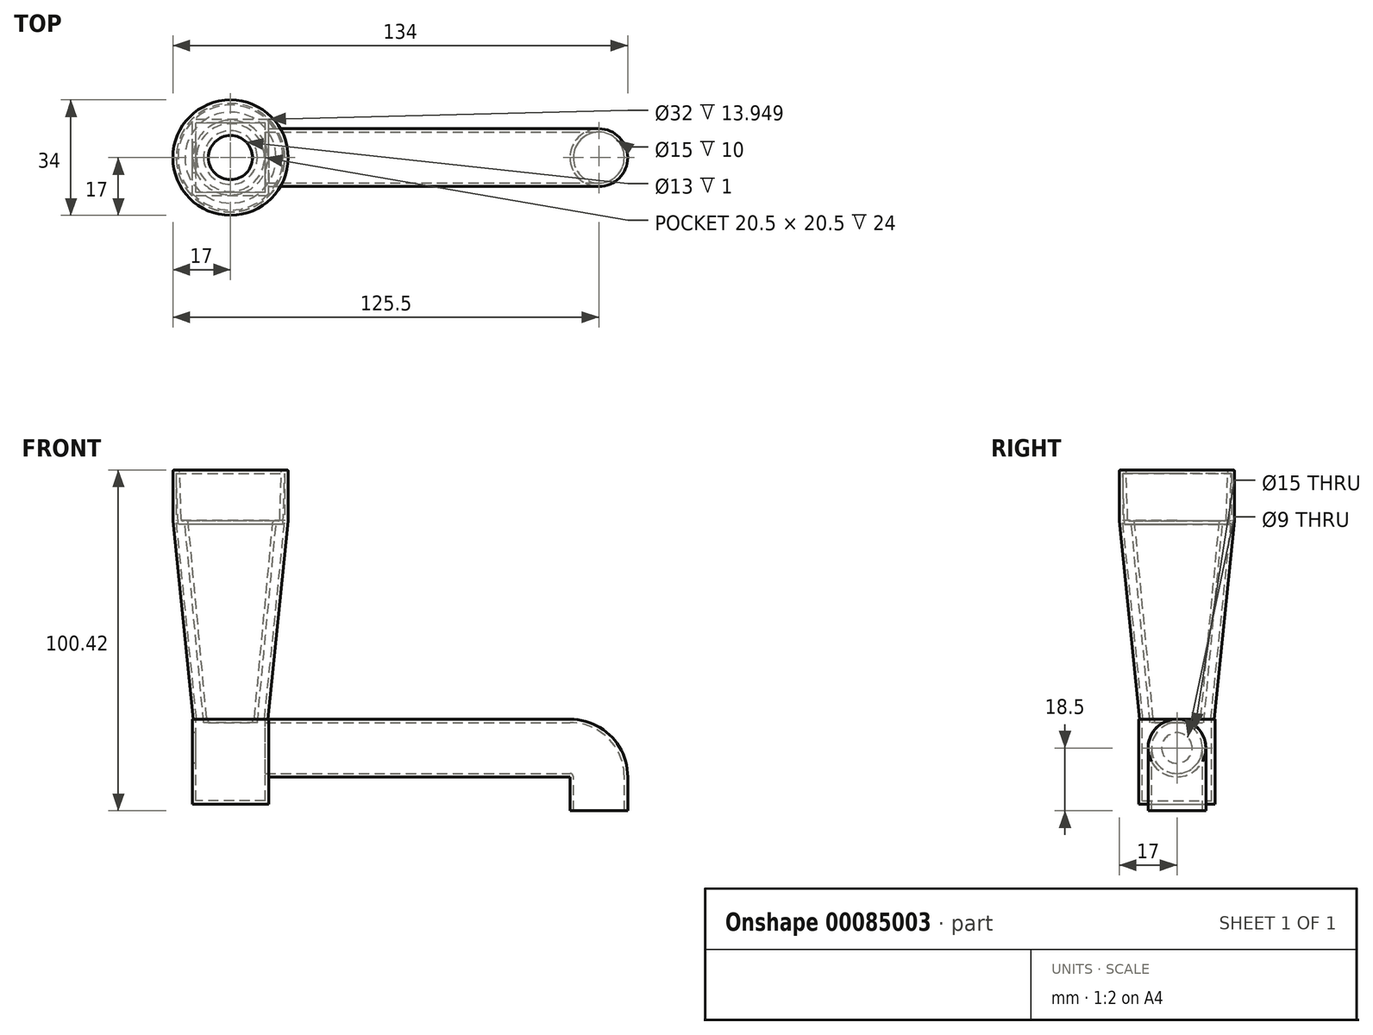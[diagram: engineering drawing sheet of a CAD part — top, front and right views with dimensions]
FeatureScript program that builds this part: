
annotation { "Feature Type Name" : "Feature", "Feature Type Description" : "" }
export const myFeature = defineFeature(function(context is Context, id is Id, definition is map)
    precondition{}
    {
        {
            var Q0;
            Q0=qCreatedBy(makeId("Front.planeOp"),FACE);
            var sketch = newSketch(context, id + "F0", { "sketchPlane" : qUnion([Q0])});
            skLineSegment(sketch, "E0", {"start": v(0, 0) * mm, "end": v(0, 73.42) * mm, "construction": true});
            skLineSegment(sketch, "E1", {"start": v(0, 73.42) * mm, "end": v(15, 73.42) * mm, "construction": true});
            skLineSegment(sketch, "E2", {"start": v(15, 73.42) * mm, "end": v(17, 73.42) * mm});
            skLineSegment(sketch, "E3", {"start": v(17, 73.42) * mm, "end": v(17, 58.42) * mm});
            skLineSegment(sketch, "E4", {"start": v(0, 58.42) * mm, "end": v(14.5, 58.42) * mm, "construction": true});
            skLineSegment(sketch, "E5", {"start": v(15, 73.42) * mm, "end": v(14.5, 58.42) * mm});
            skLineSegment(sketch, "E6", {"start": v(14.5, 58.42) * mm, "end": v(12.5, 58.42) * mm});
            skLineSegment(sketch, "E7", {"start": v(0, 0) * mm, "end": v(7, 0) * mm, "construction": true});
            skLineSegment(sketch, "E8", {"start": v(12.5, 58.42) * mm, "end": v(7, 0) * mm});
            skLineSegment(sketch, "E9", {"start": v(17, 58.42) * mm, "end": v(11, 0) * mm});
            skLineSegment(sketch, "E10", {"start": v(11, 0) * mm, "end": v(7, 0) * mm});
            skSolve(sketch);
        }
        {
            var Q0;
            Q0 = qSketchRegion(id + "F0", true);
            var Q1;
            Q1=sQuery(id+"F0.wireOp",EDGE,"E0");
            revolve(context, id + "F1", {"entities" : qUnion([Q0]), "axis" : qUnion([Q1]), "revolveType" : RevolveType.FULL});
        }
        {
            var Q0;
            Q0=qCreatedBy(makeId("Right.planeOp"),FACE);
            cPlane(context, id + "F2", {"entities" : qUnion([Q0]), "cplaneType" : CPlaneType.OFFSET, "offset" : 100 * mm, "width" : 150 * mm, "height" : 150 * mm});
        }
        {
            var Q0;
            Q0=makeQuery(id+"F1.opRevolve","SWEPT_FACE",FACE,{"disambiguationData":[OSD([sQuery(id+"F0.wireOp",EDGE,"E10")])]});
            var sketch = newSketch(context, id + "F3", { "sketchPlane" : qUnion([Q0])});
            skLineSegment(sketch, "E11.bottom", {"start": v(11.25, 11.25) * mm, "end": v(-11.25, 11.25) * mm});
            skLineSegment(sketch, "E11.top", {"start": v(11.25, -11.25) * mm, "end": v(-11.25, -11.25) * mm});
            skLineSegment(sketch, "E11.left", {"start": v(11.25, 11.25) * mm, "end": v(11.25, -11.25) * mm});
            skLineSegment(sketch, "E11.right", {"start": v(-11.25, 11.25) * mm, "end": v(-11.25, -11.25) * mm});
            skPoint(sketch, "E11.middle", {"position": v(0, 0) * mm});
            skSolve(sketch);
        }
        {
            var Q0;
            Q0 = qSketchRegion(id + "F3", true);
            extrude(context, id + "F4", {"entities" : qUnion([Q0]), "operationType" : NewBodyOperationType.ADD, "depth" : 25 * mm});
        }
        {
            var Q0;
            {var subQ0=sQuery(id+"F3.wireOp",EDGE,"E11.left");var subQ1=sQuery(id+"F3.wireOp",EDGE,"E11.top");var subQ2=sQuery(id+"F3.wireOp",EDGE,"E11.bottom");var subQ3=sQuery(id+"F3.wireOp",EDGE,"E11.right");Q0=makeQuery(id+"F4.boolean.opBoolean","SPLIT",FACE,{"disambiguationData":[TD([makeQuery(id+"F1.opRevolve","SWEPT_FACE",FACE,{"disambiguationData":[OSD([sQuery(id+"F0.wireOp",EDGE,"E9")])]})])],"derivedFrom":makeQuery(id+"F4.opExtrude","CAP_FACE",FACE,{"disambiguationData":[OSD([subQ2,subQ1,subQ0,subQ3])],"isStart":true})});}
            shell(context, id + "F5", {"entities" : qUnion([Q0]), "thickness" : 1 * mm});
        }
        {
            var Q0;
            Q0=qCreatedBy(id+"F2.planeOp",FACE);
            var sketch = newSketch(context, id + "F6", { "sketchPlane" : qUnion([Q0])});
            skCircle(sketch, "E12", {"center": v(0, -8.5) * mm, "radius": 8.5 * mm});
            skCircle(sketch, "E13", {"center": v(0, -8.5) * mm, "radius": 7.5 * mm});
            skSolve(sketch);
        }
        {
            var Q0;
            Q0 = qSketchRegion(id + "F6", true);
            extrude(context, id + "F7", {"entities" : qUnion([Q0]), "operationType" : NewBodyOperationType.ADD, "endBound" : BoundingType.UP_TO_NEXT, "oppositeDirection" : true, "depth" : 100 * mm});
        }
        {
            var Q0;
            Q0=makeQuery(id+"F1.opRevolve","SWEPT_EDGE",EDGE,{"disambiguationData":[OSD([sQuery(id+"F0.wireOp",EDGE,"E2"),sQuery(id+"F0.wireOp",EDGE,"E5")])]});
            var Q1;
            Q1=makeQuery(id+"F1.opRevolve","SWEPT_EDGE",EDGE,{"disambiguationData":[OSD([sQuery(id+"F0.wireOp",EDGE,"E2"),sQuery(id+"F0.wireOp",EDGE,"E3")])]});
            var Q2;
            Q2=makeQuery(id+"F1.opRevolve","SWEPT_EDGE",EDGE,{"disambiguationData":[OSD([sQuery(id+"F0.wireOp",EDGE,"E6"),sQuery(id+"F0.wireOp",EDGE,"E8")])]});
            var Q3;
            Q3=makeQuery(id+"F1.opRevolve","SWEPT_EDGE",EDGE,{"disambiguationData":[OSD([sQuery(id+"F0.wireOp",EDGE,"E5"),sQuery(id+"F0.wireOp",EDGE,"E6")])]});
            var Q4;
            Q4=makeQuery(id+"F1.opRevolve","SWEPT_EDGE",EDGE,{"disambiguationData":[OSD([sQuery(id+"F0.wireOp",EDGE,"E3"),sQuery(id+"F0.wireOp",EDGE,"E9")])]});
            var Q5;
            Q5=makeQuery(id+"F1.opRevolve","SWEPT_EDGE",EDGE,{"disambiguationData":[OSD([sQuery(id+"F0.wireOp",EDGE,"E9"),sQuery(id+"F0.wireOp",EDGE,"HRKtv9Oi-gNw8-WM0d-tN7Y-wkfImeTK1ehS")])]});
            var Q6;
            Q6=makeQuery(id+"F7.opExtrude","TWEAK_EDGE",EDGE,{"derivedFrom":[makeQuery(id+"F1.opRevolve","SWEPT_FACE",FACE,{"disambiguationData":[OSD([sQuery(id+"F0.wireOp",EDGE,"E9")])]}),makeQuery(id+"F6.imprint","IMPRINT",EDGE,{"derivedFrom":sQuery(id+"F6.wireOp",EDGE,"6v9iyHCW-eKOX-CDvE-R3rD-riR51iMcDnOg")})]});
            var Q7;
            Q7=makeQuery(id+"F7.opExtrude","SWEPT_FACE",FACE,{"disambiguationData":[OSD([sQuery(id+"F6.wireOp",EDGE,"6v9iyHCW-eKOX-CDvE-R3rD-riR51iMcDnOg")])]});
            fillet(context, id + "F8", {"entities" : qUnion([Q0, Q1, Q2, Q3, Q4, Q5, Q6, Q7]), "radius" : 0.5 * mm, "tangentPropagation" : true, "allowEdgeOverflow" : false});
        }
        {
            var Q0;
            Q0=makeQuery(id+"F1.opRevolve","SWEPT_EDGE",EDGE,{"disambiguationData":[OSD([sQuery(id+"F0.wireOp",EDGE,"HRKtv9Oi-gNw8-WM0d-tN7Y-wkfImeTK1ehS"),sQuery(id+"F0.wireOp",EDGE,"E10")])]});
            fillet(context, id + "F9", {"entities" : qUnion([Q0]), "radius" : 0.5 * mm, "tangentPropagation" : true, "allowEdgeOverflow" : false});
        }
        {
            var Q0;
            Q0=makeQuery(id+"F6.imprint","IMPRINT",FACE,{"disambiguationData":[TD([[makeQuery(id+"F6.imprint","IMPRINT",EDGE,{"derivedFrom":sQuery(id+"F6.wireOp",EDGE,"E12")}),1.0]])]});
            var sketch = newSketch(context, id + "F10", { "sketchPlane" : qUnion([Q0])});
            skCircle(sketch, "E14", {"center": v(0, -8.5) * mm, "radius": 7.5 * mm});
            skSolve(sketch);
        }
        {
            var Q0;
            Q0 = qSketchRegion(id + "F10", true);
            extrude(context, id + "F11", {"entities" : qUnion([Q0]), "operationType" : NewBodyOperationType.REMOVE, "oppositeDirection" : true, "depth" : 96.68 * mm});
        }
        {
            var Q0;
            Q0=qCreatedBy(makeId("Right.planeOp"),FACE);
            cPlane(context, id + "F12", {"entities" : qUnion([Q0]), "cplaneType" : CPlaneType.OFFSET, "offset" : 50 * mm, "oppositeDirection" : true, "width" : 150 * mm, "height" : 150 * mm});
        }
        {
            var Q0;
            Q0=qCreatedBy(id+"F12.planeOp",FACE);
            var sketch = newSketch(context, id + "F13", { "sketchPlane" : qUnion([Q0])});
            skCircle(sketch, "E15", {"center": v(0, -8.5) * mm, "radius": 4.5 * mm});
            skSolve(sketch);
        }
        {
            var Q0;
            Q0 = qSketchRegion(id + "F13", true);
            extrude(context, id + "F14", {"entities" : qUnion([Q0]), "operationType" : NewBodyOperationType.REMOVE, "depth" : 45.83 * mm});
        }
        {
            var Q0;
            Q0=qCreatedBy(id+"F2.planeOp",FACE);
            var sketch = newSketch(context, id + "F15", { "sketchPlane" : qUnion([Q0])});
            skLineSegment(sketch, "E16", {"start": v(-11.2, -17) * mm, "end": v(11.3, -17) * mm, "construction": true});
            skCircle(sketch, "E17", {"center": v(0, -8.5) * mm, "radius": 8.5 * mm});
            skCircle(sketch, "E18", {"center": v(0, -8.5) * mm, "radius": 7.5 * mm});
            skSolve(sketch);
        }
        {
            var Q0;
            Q0 = qSketchRegion(id + "F15", true);
            var Q1;
            Q1=sQuery(id+"F15.wireOp",EDGE,"E16");
            revolve(context, id + "F16", {"operationType" : NewBodyOperationType.ADD, "entities" : qUnion([Q0]), "axis" : qUnion([Q1]), "revolveType" : RevolveType.ONE_DIRECTION, "angle" : 90 * degree});
        }
        {
            var Q0;
            Q0=makeQuery(id+"F16.opRevolve","CAP_FACE",FACE,{"disambiguationData":[OSD([sQuery(id+"F15.wireOp",EDGE,"E17"),sQuery(id+"F15.wireOp",EDGE,"E18")])],"isStart":false});
            var sketch = newSketch(context, id + "F17", { "sketchPlane" : qUnion([Q0])});
            skCircle(sketch, "E19", {"center": v(108.5, 0) * mm, "radius": 8.5 * mm});
            skCircle(sketch, "E20", {"center": v(108.5, 0) * mm, "radius": 7.5 * mm});
            skSolve(sketch);
        }
        {
            var Q0;
            Q0 = qSketchRegion(id + "F17", true);
            extrude(context, id + "F18", {"entities" : qUnion([Q0]), "operationType" : NewBodyOperationType.ADD, "depth" : 10 * mm});
        }
        {
            var Q0;
            Q0=qCreatedBy(makeId("Top.planeOp"),FACE);
            cPlane(context, id + "F19", {"entities" : qUnion([Q0]), "cplaneType" : CPlaneType.OFFSET, "offset" : 150 * mm, "width" : 150 * mm, "height" : 150 * mm});
        }
        {
            var Q0;
            Q0=qCreatedBy(id+"F19.planeOp",FACE);
            var sketch = newSketch(context, id + "F20", { "sketchPlane" : qUnion([Q0])});
            skCircle(sketch, "E21", {"center": v(0, 0) * mm, "radius": 6.5 * mm});
            skSolve(sketch);
        }
        {
            var Q0;
            Q0 = qSketchRegion(id + "F20", true);
            extrude(context, id + "F21", {"entities" : qUnion([Q0]), "operationType" : NewBodyOperationType.REMOVE, "oppositeDirection" : true, "depth" : 155.56 * mm});
        }
    });
